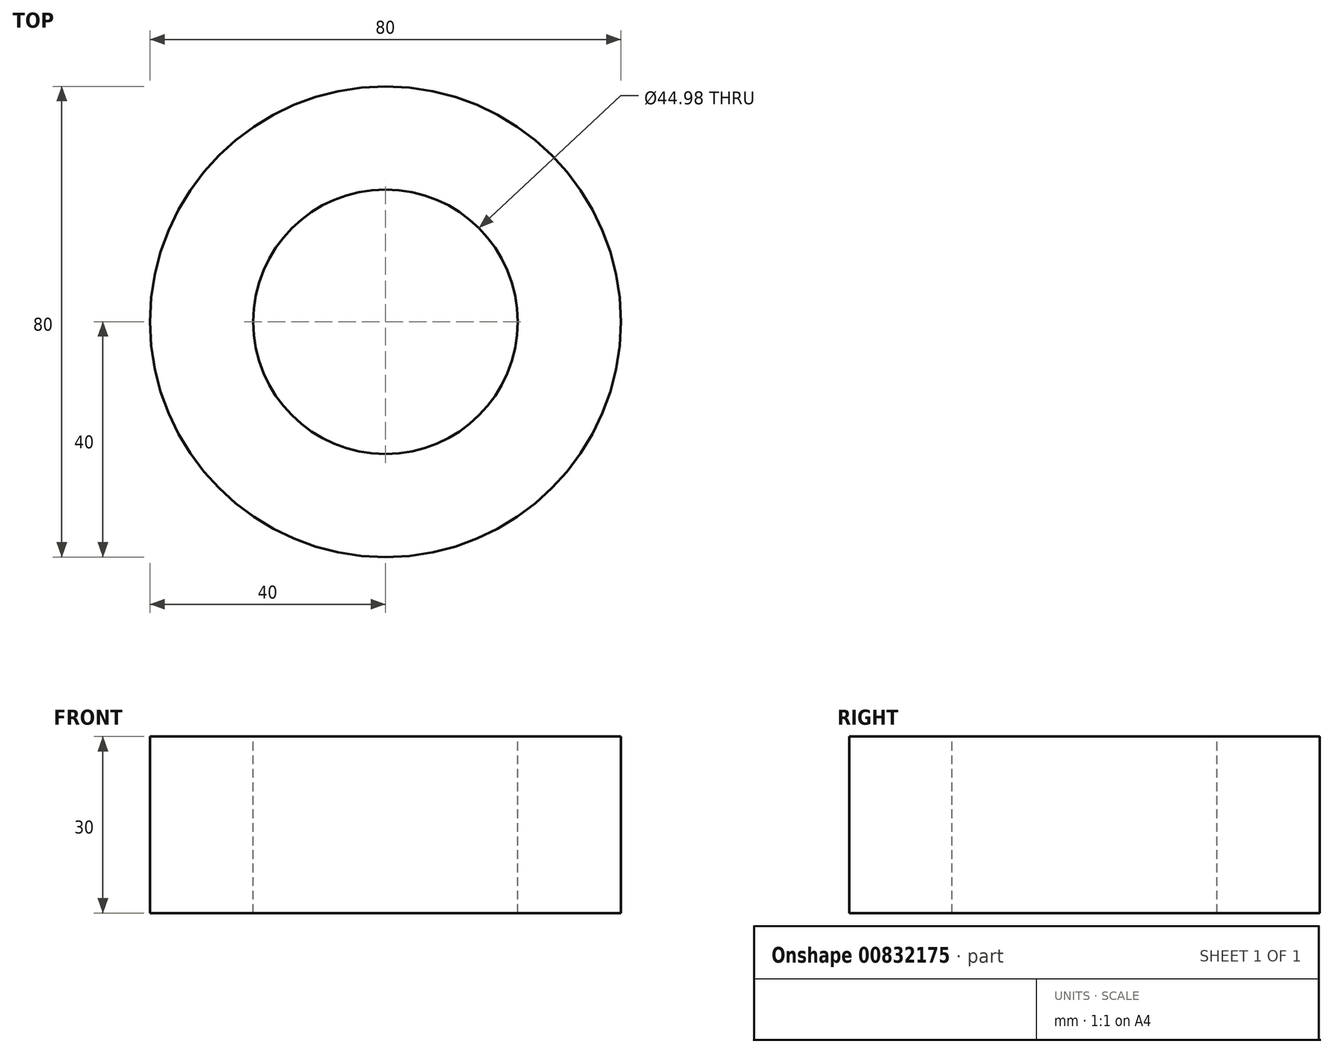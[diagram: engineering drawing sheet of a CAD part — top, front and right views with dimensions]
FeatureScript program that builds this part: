
annotation { "Feature Type Name" : "Feature", "Feature Type Description" : "" }
export const myFeature = defineFeature(function(context is Context, id is Id, definition is map)
    precondition{}
    {
        {
            var Q0;
            Q0=qCreatedBy(makeId("Top.planeOp"),FACE);
            var sketch = newSketch(context, id + "F0", { "sketchPlane" : qUnion([Q0])});
            skLineSegment(sketch, "E0", {"start": v(0, 0) * mm, "end": v(0, 40) * mm});
            skCircle(sketch, "E1", {"center": v(0, 0) * mm, "radius": 40 * mm});
            skSolve(sketch);
        }
        {
            var Q0;
            Q0=makeQuery(id+"F0.imprint","IMPRINT",FACE,{"disambiguationData":[TD([[makeQuery(id+"F0.imprint","IMPRINT",EDGE,{"derivedFrom":sQuery(id+"F0.wireOp",EDGE,"E1")}),1.0]])]});
            extrude(context, id + "F1", {"entities" : qUnion([Q0]), "depth" : 30 * mm, "offsetDistance" : 25 * mm});
        }
        {
            var Q0;
            Q0=makeQuery(id+"F1.opExtrude","CAP_FACE",FACE,{"disambiguationData":[OSD([sQuery(id+"F0.wireOp",EDGE,"E1")])],"isStart":false});
            var sketch = newSketch(context, id + "F2", { "sketchPlane" : qUnion([Q0])});
            skCircle(sketch, "E2", {"center": v(0, 0) * mm, "radius": 22.5 * mm});
            skSolve(sketch);
        }
        {
            var Q0;
            Q0=makeQuery(id+"F2.imprint","IMPRINT",FACE,{"disambiguationData":[TD([[makeQuery(id+"F2.imprint","IMPRINT",EDGE,{"derivedFrom":sQuery(id+"F2.wireOp",EDGE,"E2")}),1.0]])]});
            extrude(context, id + "F3", {"entities" : qUnion([Q0]), "operationType" : NewBodyOperationType.REMOVE, "endBound" : BoundingType.THROUGH_ALL, "oppositeDirection" : true, "depth" : 25 * mm, "offsetDistance" : 25 * mm});
        }
        {
            var Q0;
            Q0=makeQuery(id+"F1.opExtrude","SWEPT_BODY",BODY,{"disambiguationData":[OSD([sQuery(id+"F0.wireOp",EDGE,"E1")])]});
            transform(context, id + "F4", {"entities" : qUnion([Q0]), "transformType" : TransformType.TRANSLATION_3D, "dx" : 0 * mm, "dy" : 0 * mm, "dz" : 0 * mm, "makeCopy" : true});
        }
        {
            var Q0;
            Q0=makeQuery(id+"F4.opPattern","COPY",BODY,{"derivedFrom":makeQuery(id+"F1.opExtrude","SWEPT_BODY",BODY,{"disambiguationData":[OSD([sQuery(id+"F0.wireOp",EDGE,"E1")])]}),"instanceName":"1"});
            deleteBodies(context, id + "F5", {"entities" : qUnion([Q0])});
        }
    });
